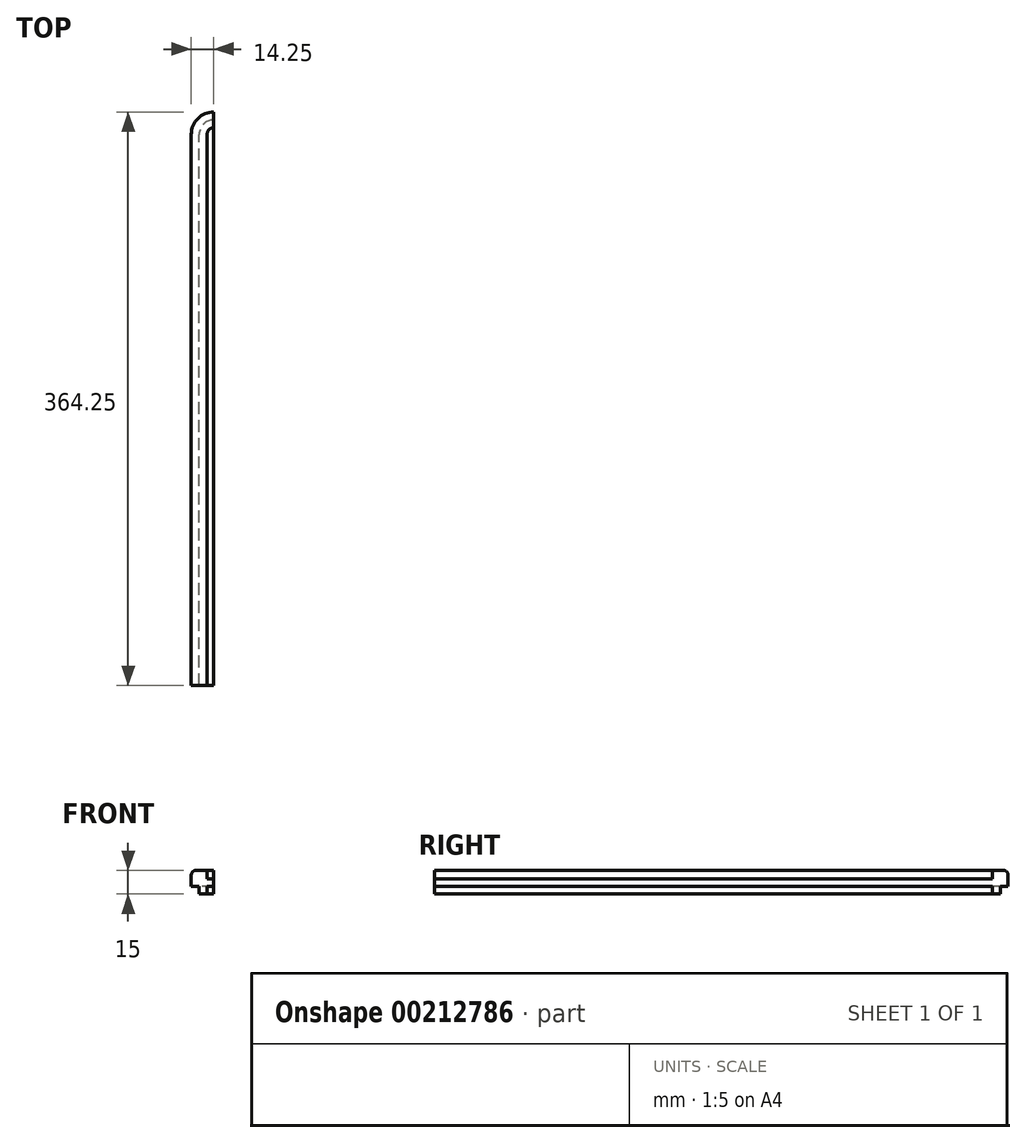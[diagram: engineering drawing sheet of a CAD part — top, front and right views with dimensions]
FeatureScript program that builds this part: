
annotation { "Feature Type Name" : "Feature", "Feature Type Description" : "" }
export const myFeature = defineFeature(function(context is Context, id is Id, definition is map)
    precondition{}
    {
        {
            var Q0;
            Q0=qCreatedBy(makeId("Front.planeOp"),FACE);
            var sketch = newSketch(context, id + "F0", { "sketchPlane" : qUnion([Q0])});
            skLineSegment(sketch, "E0.bottom", {"start": v(-50.92, 48.87) * mm, "end": v(-43.92, 48.87) * mm});
            skLineSegment(sketch, "E0.top", {"start": v(-53.92, 38.87) * mm, "end": v(-43.92, 38.87) * mm});
            skLineSegment(sketch, "E0.left", {"start": v(-53.92, 45.87) * mm, "end": v(-53.92, 38.87) * mm});
            skLineSegment(sketch, "E0.right", {"start": v(-43.92, 48.87) * mm, "end": v(-43.92, 38.87) * mm});
            skPoint(sketch, "E1.visualSharp", {"position": v(-53.92, 48.87) * mm});
            skArc(sketch, "E1.filletArc", {"start": v(-50.92, 48.87) * mm, "mid": v(-53.04, 48) * mm, "end": v(-53.92, 45.87) * mm});
            skLineSegment(sketch, "E2.bottom", {"start": v(-43.92, 38.87) * mm, "end": v(-48.92, 38.87) * mm});
            skLineSegment(sketch, "E2.top", {"start": v(-43.92, 33.87) * mm, "end": v(-48.92, 33.87) * mm});
            skLineSegment(sketch, "E2.left", {"start": v(-43.92, 38.87) * mm, "end": v(-43.92, 33.87) * mm});
            skLineSegment(sketch, "E2.right", {"start": v(-48.92, 38.87) * mm, "end": v(-48.92, 33.87) * mm});
            skLineSegment(sketch, "E3.bottom", {"start": v(-43.92, 38.87) * mm, "end": v(-39.67, 38.87) * mm});
            skLineSegment(sketch, "E3.top", {"start": v(-43.92, 43.38) * mm, "end": v(-39.67, 43.38) * mm});
            skLineSegment(sketch, "E3.left", {"start": v(-43.92, 38.87) * mm, "end": v(-43.92, 43.38) * mm});
            skLineSegment(sketch, "E3.right", {"start": v(-39.67, 38.87) * mm, "end": v(-39.67, 43.38) * mm});
            skSolve(sketch);
        }
        {
            var Q0;
            Q0 = qSketchRegion(id + "F0", true);
            extrude(context, id + "F1", {"entities" : qUnion([Q0]), "depth" : 350 * mm});
        }
        {
            var Q0;
            Q0 = qSketchRegion(id + "F0", true);
            var Q1;
            Q1=sQuery(id+"F0.wireOp",EDGE,"E3.right");
            revolve(context, id + "F2", {"operationType" : NewBodyOperationType.ADD, "entities" : qUnion([Q0]), "axis" : qUnion([Q1]), "revolveType" : RevolveType.ONE_DIRECTION, "oppositeDirection" : true, "angle" : 90 * degree});
        }
    });
